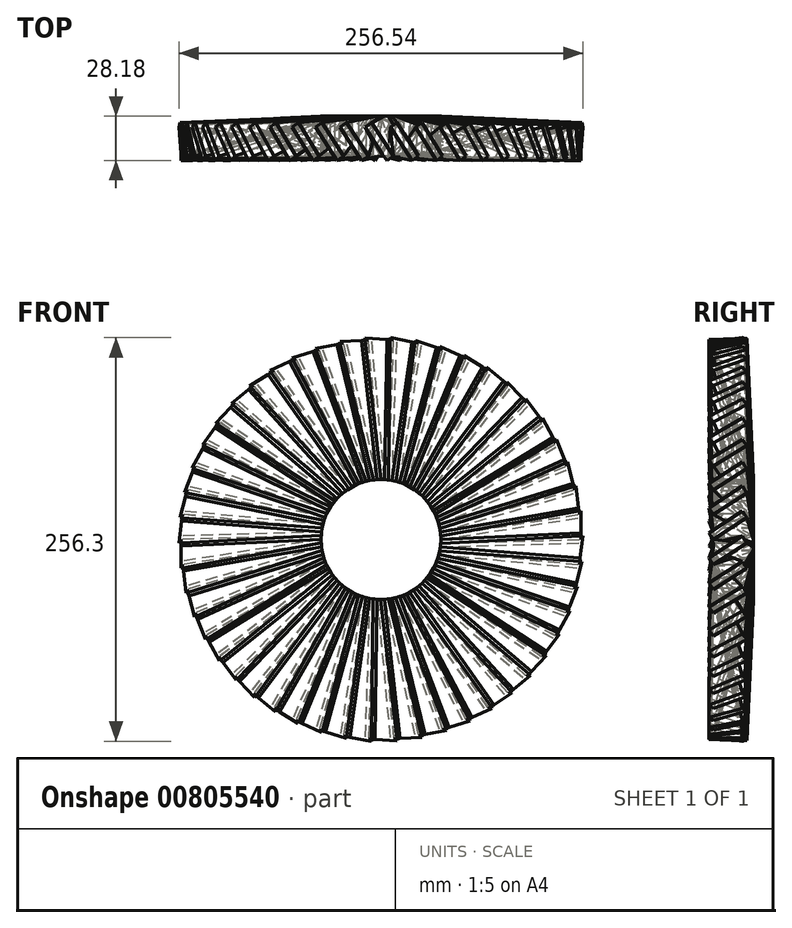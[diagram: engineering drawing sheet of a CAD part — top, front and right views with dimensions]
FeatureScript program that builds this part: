
annotation { "Feature Type Name" : "Feature", "Feature Type Description" : "" }
export const myFeature = defineFeature(function(context is Context, id is Id, definition is map)
    precondition{}
    {
        {
            var Q0;
            Q0=qCreatedBy(makeId("Front.planeOp"),FACE);
            var sketch = newSketch(context, id + "F0", { "sketchPlane" : qUnion([Q0])});
            skCircle(sketch, "E0", {"center": v(0, 0) * mm, "radius": 38.1 * mm});
            skSolve(sketch);
        }
        {
            var Q0;
            Q0=makeQuery(id+"F0.imprint","IMPRINT",FACE,{"disambiguationData":[TD([[makeQuery(id+"F0.imprint","IMPRINT",EDGE,{"derivedFrom":sQuery(id+"F0.wireOp",EDGE,"E0")}),1.0]])]});
            extrude(context, id + "F1", {"entities" : qUnion([Q0]), "depth" : 25.4 * mm, "offsetDistance" : 25.4 * mm});
        }
        {
            var Q0;
            Q0=qCreatedBy(makeId("Right.planeOp"),FACE);
            cPlane(context, id + "F2", {"entities" : qUnion([Q0]), "cplaneType" : CPlaneType.OFFSET, "offset" : 38.1 * mm, "width" : 152.4 * mm, "height" : 152.4 * mm});
        }
        {
            var Q0;
            Q0=qCreatedBy(id+"F2.planeOp",FACE);
            var sketch = newSketch(context, id + "F3", { "sketchPlane" : qUnion([Q0])});
            skLineSegment(sketch, "E1", {"start": v(0, 0) * mm, "end": v(0, 2.54) * mm});
            skLineSegment(sketch, "E2", {"start": v(0, 2.54) * mm, "end": v(-25.4, 2.54) * mm});
            skLineSegment(sketch, "E3", {"start": v(-25.4, 2.54) * mm, "end": v(-25.4, 0) * mm});
            skLineSegment(sketch, "E4", {"start": v(-25.4, 0) * mm, "end": v(-25.4, -2.54) * mm});
            skLineSegment(sketch, "E5", {"start": v(-25.4, -2.54) * mm, "end": v(0, -2.54) * mm});
            skLineSegment(sketch, "E6", {"start": v(0, -2.54) * mm, "end": v(0, 0) * mm});
            skSolve(sketch);
        }
        {
            var Q0;
            Q0=qCreatedBy(id+"F2.planeOp",FACE);
            cPlane(context, id + "F4", {"entities" : qUnion([Q0]), "cplaneType" : CPlaneType.OFFSET, "offset" : 88.9 * mm, "width" : 152.4 * mm, "height" : 152.4 * mm});
        }
        {
            var Q0;
            Q0=qCreatedBy(id+"F4.planeOp",FACE);
            var sketch = newSketch(context, id + "F5", { "sketchPlane" : qUnion([Q0])});
            skLineSegment(sketch, "E7", {"start": v(-25.4, 0) * mm, "end": v(-28.18, 4.25) * mm});
            skLineSegment(sketch, "E8", {"start": v(-28.18, 4.25) * mm, "end": v(-6.92, 18.15) * mm});
            skLineSegment(sketch, "E9", {"start": v(-6.92, 18.15) * mm, "end": v(-4.14, 13.9) * mm});
            skLineSegment(sketch, "E10", {"start": v(-4.14, 13.9) * mm, "end": v(-25.4, 0) * mm});
            skSolve(sketch);
        }
        {
            var Q1;
            Q1=makeQuery(id+"F3.imprint","IMPRINT",FACE,{"disambiguationData":[TD([[makeQuery(id+"F3.imprint","IMPRINT",EDGE,{"derivedFrom":sQuery(id+"F3.wireOp",EDGE,"E1")}),1.0]])]});
            var Q2;
            Q2=makeQuery(id+"F5.imprint","IMPRINT",FACE,{"disambiguationData":[TD([[makeQuery(id+"F5.imprint","IMPRINT",EDGE,{"derivedFrom":sQuery(id+"F5.wireOp",EDGE,"E7")}),-1.0]])]});
            loft(context, id + "F6", {"operationType" : NewBodyOperationType.ADD, "sheetProfilesArray" : [{ "sheetProfileEntities" : qUnion([Q1]) }, { "sheetProfileEntities" : qUnion([Q2]) }]});
        }
        {
            var Q0;
            Q0=makeQuery(id+"F6.opLoft","SWEPT_BODY",BODY,{"disambiguationData":[OSD([makeQuery(id+"F3.imprint","IMPRINT",FACE,{"disambiguationData":[TD([[makeQuery(id+"F3.imprint","IMPRINT",EDGE,{"derivedFrom":sQuery(id+"F3.wireOp",EDGE,"E1")}),1.0]])]}),makeQuery(id+"F5.imprint","IMPRINT",FACE,{"disambiguationData":[TD([[makeQuery(id+"F5.imprint","IMPRINT",EDGE,{"derivedFrom":sQuery(id+"F5.wireOp",EDGE,"E7")}),-1.0]])]})])]});
            var Q1;
            Q1=makeQuery(id+"F1.opExtrude","SWEPT_FACE",FACE,{"disambiguationData":[OSD([sQuery(id+"F0.wireOp",EDGE,"E0")])]});
            circularPattern(context, id + "F7", {"entities" : qUnion([Q0]), "axis" : qUnion([Q1]), "angle" : 360 * degree, "instanceCount" : 50, "equalSpace" : true});
        }
    });
